# Revit family: Skylight_Fakro_FVE
name_source: partatom
category: Generic Models
units: mm (PartAtom-declared; Revit-internal decimal feet)

## family parameters
Always vertical = No
Can host rebar = No
Classification Number = 23.30.30.14
Cut with Voids When Loaded = No
Host = Roof
Maintain Annotation Orientation = No
Part Type = Normal
Room Calculation Point = No
Round Connector Dimension = Use Diameter
Shared = No

## types (10) — shared parameters
Assembly Code = B3020110
Keynote = 08 62 00
Manufacturer = Fakro USA
Manufacturer Fax = 630-543-1011
Manufacturer Website = http://www.fakrousa.com
Mechanism Height = 90 mm  [stored 0.295276 ft]
Model = FVE
Product Data = http://www.fakrousa.com
Revision = R1_2016-01
Sales Information = http://www.fakrousa.com
URL = http://www.fakrousa.com
zero-valued in all types: Cost, Default Elevation, Expected Lifespan (Years), Maintenance Schedule (Months), Warranty Duration (Years)

## per-type parameters (varying)
| type | Blend Length | Description | Sash Length | Sash Width | Screen Height | Screen Width | Side Apron Length | Unit Height | Unit Width | Upper Apron Length |
| 48x46 | 1128 mm  [stored 3.70079 ft] | Fakro FVE Skylight - 48x46 | 1099 mm  [stored 3.60564 ft] | 1150 mm  [stored 3.77297 ft] | 1053 mm | 1128 mm  [stored 3.70079 ft] | 1150 mm  [stored 3.77297 ft] | 1178 mm  [stored 3.86483 ft] | 1232 mm  [stored 4.04199 ft] | 1172 mm  [stored 3.84514 ft] |
| 48x27 | 1128 mm  [stored 3.70079 ft] | Fakro FVE Skylight - 48x27 | 620 mm  [stored 2.03412 ft] | 1150 mm  [stored 3.77297 ft] | 574 mm | 1128 mm  [stored 3.70079 ft] | 671 mm  [stored 2.20144 ft] | 699 mm  [stored 2.29331 ft] | 1232 mm  [stored 4.04199 ft] | 1172 mm  [stored 3.84514 ft] |
| 32x55 | 722 mm | Fakro FVE Skylight - 32x55 | 1318 mm  [stored 4.32415 ft] | 744 mm | 1272 mm | 722 mm | 1369 mm | 1397 mm  [stored 4.58333 ft] | 826 mm  [stored 2.70997 ft] | 766 mm |
| 32x46 | 722 mm | Fakro FVE Skylight - 32x46 | 1099 mm  [stored 3.60564 ft] | 744 mm | 1053 mm | 722 mm | 1150 mm  [stored 3.77297 ft] | 1178 mm  [stored 3.86483 ft] | 826 mm  [stored 2.70997 ft] | 766 mm |
| 32x38 | 722 mm | Fakro FVE Skylight - 32x38 | 899 mm  [stored 2.94948 ft] | 744 mm | 853 mm | 722 mm | 950 mm  [stored 3.1168 ft] | 978 mm  [stored 3.20866 ft] | 826 mm  [stored 2.70997 ft] | 766 mm |
| 24x70 | 519 mm | Fakro FVE Skylight - 24x70 | 1718 mm  [stored 5.63648 ft] | 541 mm | 1672 mm | 519 mm | 1769 mm | 1797 mm  [stored 5.89567 ft] | 623 mm  [stored 2.04396 ft] | 563 mm |
| 24x55 | 519 mm | Fakro FVE Skylight - 24x55 | 1318 mm  [stored 4.32415 ft] | 541 mm | 1272 mm | 519 mm | 1369 mm | 1397 mm  [stored 4.58333 ft] | 623 mm  [stored 2.04396 ft] | 563 mm |
| 24x46 | 519 mm | Fakro FVE Skylight - 24x46 | 1099 mm  [stored 3.60564 ft] | 541 mm | 1053 mm | 519 mm | 1150 mm  [stored 3.77297 ft] | 1178 mm  [stored 3.86483 ft] | 623 mm  [stored 2.04396 ft] | 563 mm |
| 24x38 | 519 mm | Fakro FVE Skylight - 24x38 | 899 mm  [stored 2.94948 ft] | 541 mm | 853 mm | 519 mm | 950 mm  [stored 3.1168 ft] | 978 mm  [stored 3.20866 ft] | 623 mm  [stored 2.04396 ft] | 563 mm |
| 24x27 | 519 mm | Fakro FVE Skylight - 24x27 | 620 mm  [stored 2.03412 ft] | 541 mm | 574 mm | 519 mm | 671 mm  [stored 2.20144 ft] | 699 mm  [stored 2.29331 ft] | 623 mm  [stored 2.04396 ft] | 563 mm |

note: [stored X ft] marks values corroborated as IEEE doubles in the binary element streams (Revit-internal decimal feet)

## geometry (parser evidence)
native form markers: Blend x11
no freeform markers — native parametric forms only
